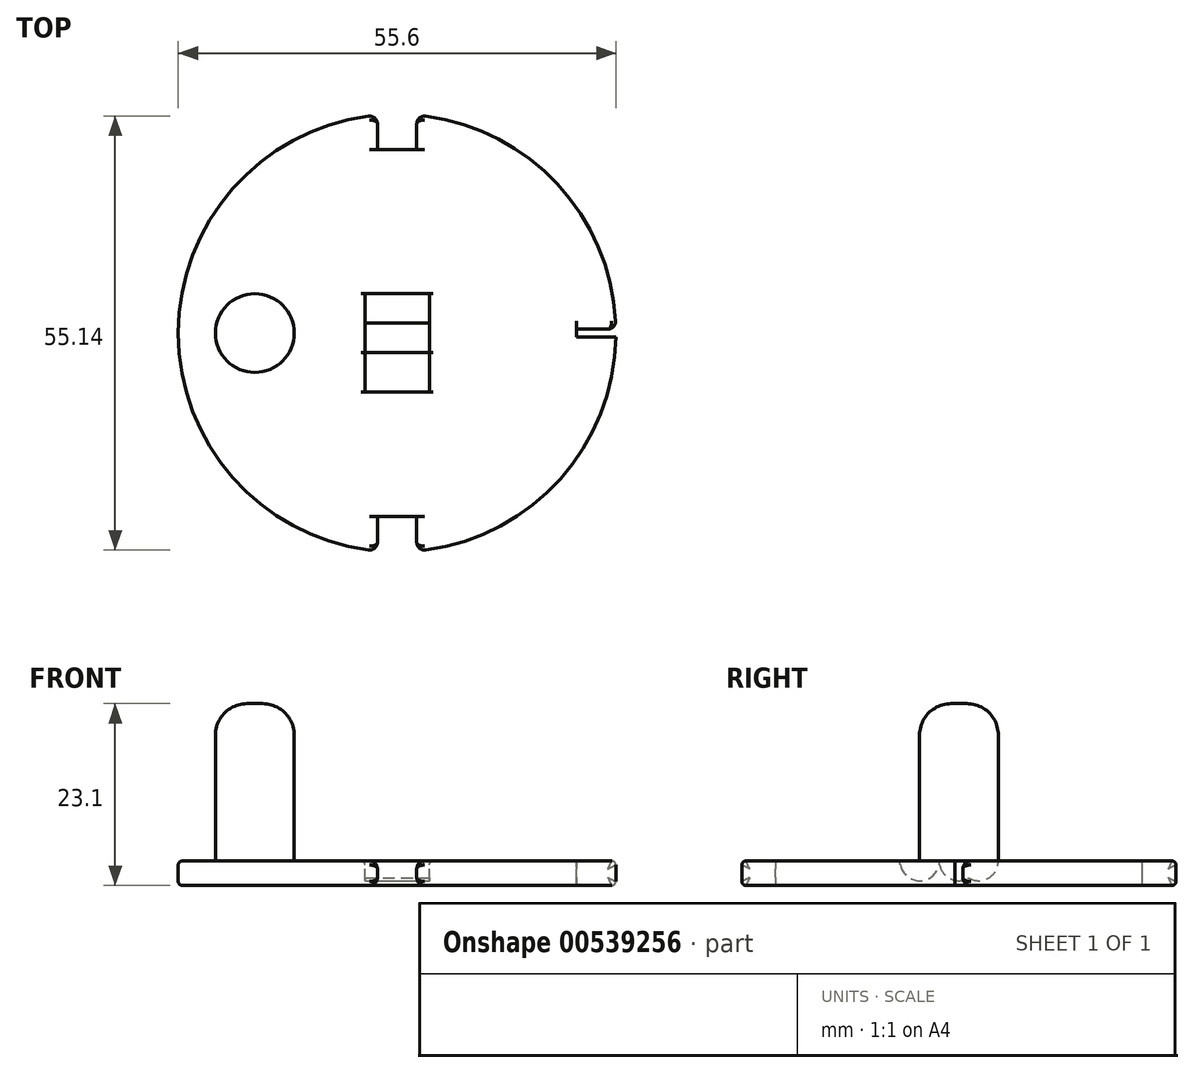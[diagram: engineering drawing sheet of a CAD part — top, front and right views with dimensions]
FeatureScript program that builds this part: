
annotation { "Feature Type Name" : "Feature", "Feature Type Description" : "" }
export const myFeature = defineFeature(function(context is Context, id is Id, definition is map)
    precondition{}
    {
        {
            var Q0;
            Q0=qCreatedBy(makeId("Top.planeOp"),FACE);
            var sketch = newSketch(context, id + "F0", { "sketchPlane" : qUnion([Q0])});
            skCircle(sketch, "E0", {"center": v(0, 0) * mm, "radius": 27.8 * mm});
            skSolve(sketch);
        }
        {
            var Q0;
            Q0=qSketchRegion(id+"F0",true);
            extrude(context, id + "F1", {"entities" : qUnion([Q0]), "depth" : 3.1 * mm});
        }
        {
            var Q0;
            Q0=makeQuery(id+"F1.opExtrude","CAP_FACE",FACE,{"disambiguationData":[OSD([sQuery(id+"F0.wireOp",EDGE,"E0")])],"isStart":false});
            var Q1;
            Q1=makeQuery(id+"F1.opExtrude","CAP_FACE",FACE,{"disambiguationData":[OSD([sQuery(id+"F0.wireOp",EDGE,"E0")])],"isStart":true});
            fillet(context, id + "F2", {"entities" : qUnion([Q0, Q1]), "radius" : 0.5 * mm, "tangentPropagation" : true, "allowEdgeOverflow" : false});
        }
        {
            var Q0;
            Q0=makeQuery(id+"F1.opExtrude","CAP_FACE",FACE,{"disambiguationData":[OSD([sQuery(id+"F0.wireOp",EDGE,"E0")])],"isStart":false});
            var sketch = newSketch(context, id + "F3", { "sketchPlane" : qUnion([Q0])});
            skLineSegment(sketch, "E1.bottom", {"start": v(-2.5, 28.3) * mm, "end": v(2.5, 28.3) * mm});
            skLineSegment(sketch, "E1.top", {"start": v(-2.5, 23.3) * mm, "end": v(2.5, 23.3) * mm});
            skLineSegment(sketch, "E1.left", {"start": v(-2.5, 28.3) * mm, "end": v(-2.5, 23.3) * mm});
            skLineSegment(sketch, "E1.right", {"start": v(2.5, 28.3) * mm, "end": v(2.5, 23.3) * mm});
            skPoint(sketch, "E1.middle", {"position": v(0, 25.8) * mm});
            skLineSegment(sketch, "E2.MirrorCS", {"start": v(-2.5, -23.3) * mm, "end": v(2.5, -23.3) * mm});
            skLineSegment(sketch, "E3.MirrorCS", {"start": v(-2.5, -28.3) * mm, "end": v(2.5, -28.3) * mm});
            skLineSegment(sketch, "E4.MirrorCS", {"start": v(-2.5, -28.3) * mm, "end": v(-2.5, -23.3) * mm});
            skPoint(sketch, "E5.MirrorP", {"position": v(0, -25.8) * mm});
            skLineSegment(sketch, "E6.MirrorCS", {"start": v(2.5, -28.3) * mm, "end": v(2.5, -23.3) * mm});
            skSolve(sketch);
        }
        {
            var Q0;
            Q0=qSketchRegion(id+"F3",true);
            extrude(context, id + "F4", {"entities" : qUnion([Q0]), "operationType" : NewBodyOperationType.REMOVE, "endBound" : BoundingType.THROUGH_ALL, "oppositeDirection" : true, "depth" : 25 * mm, "offsetDistance" : 25 * mm});
        }
        {
            var Q0;
            Q0=makeQuery(id+"F4.boolean.opBoolean","INTERSECT",EDGE,{"derivedFrom":[makeQuery(id+"F1.opExtrude","SWEPT_FACE",FACE,{"disambiguationData":[OSD([sQuery(id+"F0.wireOp",EDGE,"E0")])]}),makeQuery(id+"F4.opExtrude","SWEPT_FACE",FACE,{"disambiguationData":[OSD([sQuery(id+"F3.wireOp",EDGE,"E4.MirrorCS")])]})]});
            var Q1;
            Q1=makeQuery(id+"F4.boolean.opBoolean","INTERSECT",EDGE,{"derivedFrom":[makeQuery(id+"F1.opExtrude","SWEPT_FACE",FACE,{"disambiguationData":[OSD([sQuery(id+"F0.wireOp",EDGE,"E0")])]}),makeQuery(id+"F4.opExtrude","SWEPT_FACE",FACE,{"disambiguationData":[OSD([sQuery(id+"F3.wireOp",EDGE,"E6.MirrorCS")])]})]});
            var Q2;
            Q2=makeQuery(id+"F4.boolean.opBoolean","INTERSECT",EDGE,{"derivedFrom":[makeQuery(id+"F1.opExtrude","SWEPT_FACE",FACE,{"disambiguationData":[OSD([sQuery(id+"F0.wireOp",EDGE,"E0")])]}),makeQuery(id+"F4.opExtrude","SWEPT_FACE",FACE,{"disambiguationData":[OSD([sQuery(id+"F3.wireOp",EDGE,"E1.left")])]})]});
            var Q3;
            Q3=makeQuery(id+"F4.boolean.opBoolean","INTERSECT",EDGE,{"derivedFrom":[makeQuery(id+"F1.opExtrude","SWEPT_FACE",FACE,{"disambiguationData":[OSD([sQuery(id+"F0.wireOp",EDGE,"E0")])]}),makeQuery(id+"F4.opExtrude","SWEPT_FACE",FACE,{"disambiguationData":[OSD([sQuery(id+"F3.wireOp",EDGE,"E1.right")])]})]});
            fillet(context, id + "F5", {"entities" : qUnion([Q0, Q1, Q2, Q3]), "radius" : 1 * mm, "tangentPropagation" : true, "allowEdgeOverflow" : false});
        }
        {
            var Q0;
            Q0=makeQuery(id+"F1.opExtrude","CAP_FACE",FACE,{"disambiguationData":[OSD([sQuery(id+"F0.wireOp",EDGE,"E0")])],"isStart":false});
            var sketch = newSketch(context, id + "F6", { "sketchPlane" : qUnion([Q0])});
            skCircle(sketch, "E7", {"center": v(-18.07, 0) * mm, "radius": 5 * mm});
            skSolve(sketch);
        }
        {
            var Q0;
            Q0=qSketchRegion(id+"F6",true);
            extrude(context, id + "F7", {"entities" : qUnion([Q0]), "operationType" : NewBodyOperationType.ADD, "depth" : 20 * mm, "offsetDistance" : 25 * mm});
        }
        {
            var Q0;
            Q0=makeQuery(id+"F7.opExtrude","CAP_FACE",FACE,{"disambiguationData":[OSD([sQuery(id+"F6.wireOp",EDGE,"E7")])],"isStart":false});
            var Q1;
            Q1=makeQuery(id+"F7.opExtrude","CAP_EDGE",EDGE,{"disambiguationData":[OSD([sQuery(id+"F6.wireOp",EDGE,"E7")])],"isStart":true});
            fillet(context, id + "F8", {"entities" : qUnion([Q0, Q1]), "radius" : 4 * mm, "tangentPropagation" : true, "allowEdgeOverflow" : false});
        }
        {
            var Q0;
            Q0=makeQuery(id+"F1.opExtrude","CAP_FACE",FACE,{"disambiguationData":[OSD([sQuery(id+"F0.wireOp",EDGE,"E0")])],"isStart":false});
            var sketch = newSketch(context, id + "F9", { "sketchPlane" : qUnion([Q0])});
            skLineSegment(sketch, "E8.bottom", {"start": v(27.8, -0.5) * mm, "end": v(22.8, -0.5) * mm});
            skLineSegment(sketch, "E8.top", {"start": v(27.8, 0.5) * mm, "end": v(22.8, 0.5) * mm});
            skLineSegment(sketch, "E8.left", {"start": v(27.8, -0.5) * mm, "end": v(27.8, 0.5) * mm});
            skLineSegment(sketch, "E8.right", {"start": v(22.8, -0.5) * mm, "end": v(22.8, 0.5) * mm});
            skPoint(sketch, "E8.middle", {"position": v(25.3, 0) * mm});
            skPoint(sketch, "E8.middle.positionSnap0", {"position": v(27.3, 0) * mm});
            skPoint(sketch, "E8.centerSnap0", {"position": v(27.3, 0) * mm});
            skSolve(sketch);
        }
        {
            var Q0;
            {var subQ0=sQuery(id+"F9.wireOp",EDGE,"E8.right");Q0=makeQuery(id+"F9.imprint","IMPRINT",FACE,{"disambiguationData":[TD([[makeQuery(id+"F9.imprint","IMPRINT",EDGE,{"derivedFrom":subQ0}),-1.0]])]});}
            var Q1;
            Q1=qSketchRegion(id+"F9",true);
            extrude(context, id + "F10", {"entities" : qUnion([Q0, Q1]), "operationType" : NewBodyOperationType.REMOVE, "endBound" : BoundingType.THROUGH_ALL, "oppositeDirection" : true, "depth" : 25 * mm, "offsetDistance" : 25 * mm});
        }
        {
            var Q0;
            Q0=makeQuery(id+"F10.boolean.opBoolean","COPY",EDGE,{"derivedFrom":makeQuery(id+"F10.opExtrude","SWEPT_EDGE",EDGE,{"disambiguationData":[OSD([sQuery(id+"F9.wireOp",EDGE,"E8.top"),sQuery(id+"F9.wireOp",EDGE,"E8.left")])]})});
            var Q1;
            Q1=makeQuery(id+"F10.boolean.opBoolean","COPY",EDGE,{"derivedFrom":makeQuery(id+"F10.opExtrude","SWEPT_EDGE",EDGE,{"disambiguationData":[OSD([sQuery(id+"F9.wireOp",EDGE,"E8.bottom"),sQuery(id+"F9.wireOp",EDGE,"E8.left")])]})});
            fillet(context, id + "F11", {"entities" : qUnion([Q0, Q1]), "radius" : 1 * mm, "tangentPropagation" : true, "allowEdgeOverflow" : false});
        }
        {
            var Q0;
            Q0=qCreatedBy(makeId("Right.planeOp"),FACE);
            var sketch = newSketch(context, id + "F12", { "sketchPlane" : qUnion([Q0])});
            skCircle(sketch, "E9", {"center": v(0, 3.1) * mm, "radius": 2.5 * mm});
            skCircle(sketch, "E10", {"center": v(2.5, 3.1) * mm, "radius": 2.5 * mm});
            skCircle(sketch, "E11", {"center": v(-5, 3.1) * mm, "radius": 2.5 * mm});
            skSolve(sketch);
        }
        {
            var Q0;
            Q0 = qSketchRegion(id + "F12", true);
            extrude(context, id + "F13", {"entities" : qUnion([Q0]), "operationType" : NewBodyOperationType.REMOVE, "oppositeDirection" : true, "depth" : 4.1 * mm, "offsetDistance" : 25 * mm, "hasSecondDirection" : true, "secondDirectionOppositeDirection" : false, "secondDirectionDepth" : 4.1 * mm});
        }
        {
            var Q0;
            Q0=makeQuery(id+"F13.boolean.opBoolean","INTERSECT",EDGE,{"derivedFrom":[makeQuery(id+"F1.opExtrude","CAP_FACE",FACE,{"disambiguationData":[OSD([sQuery(id+"F0.wireOp",EDGE,"E0")])],"isStart":false}),makeQuery(id+"F13.opExtrude","CAP_FACE",FACE,{"disambiguationData":[OSD([sQuery(id+"F12.wireOp",EDGE,"E9")])],"isStart":true})]});
            var Q1;
            Q1=makeQuery(id+"F13.boolean.opBoolean","INTERSECT",EDGE,{"disambiguationData":[OD(0.0)],"derivedFrom":[makeQuery(id+"F1.opExtrude","CAP_FACE",FACE,{"disambiguationData":[OSD([sQuery(id+"F0.wireOp",EDGE,"E0")])],"isStart":false}),makeQuery(id+"F13.opExtrude","SWEPT_FACE",FACE,{"disambiguationData":[OSD([sQuery(id+"F12.wireOp",EDGE,"E9")])]})]});
            var Q2;
            Q2=makeQuery(id+"F13.boolean.opBoolean","INTERSECT",EDGE,{"disambiguationData":[OD(1.0)],"derivedFrom":[makeQuery(id+"F1.opExtrude","CAP_FACE",FACE,{"disambiguationData":[OSD([sQuery(id+"F0.wireOp",EDGE,"E0")])],"isStart":false}),makeQuery(id+"F13.opExtrude","SWEPT_FACE",FACE,{"disambiguationData":[OSD([sQuery(id+"F12.wireOp",EDGE,"E9")])]})]});
            var Q3;
            Q3=makeQuery(id+"F13.boolean.opBoolean","INTERSECT",EDGE,{"derivedFrom":[makeQuery(id+"F1.opExtrude","CAP_FACE",FACE,{"disambiguationData":[OSD([sQuery(id+"F0.wireOp",EDGE,"E0")])],"isStart":false}),makeQuery(id+"F13.opExtrude","CAP_FACE",FACE,{"disambiguationData":[OSD([sQuery(id+"F12.wireOp",EDGE,"E9")])],"isStart":false})]});
            fillet(context, id + "F14", {"entities" : qUnion([Q0, Q1, Q2, Q3]), "radius" : 0.5 * mm, "tangentPropagation" : true, "allowEdgeOverflow" : false});
        }
    });
